# Revit family: WashBasin-Monoblock-Vitra_PluralSeries_7814B003-0001
name_source: partatom
category: Plumbing Fixtures
revit_build: Autodesk Revit 2017 (Build: 20160225_1515(x64)
units: mm (PartAtom-declared; Revit-internal decimal feet)

## family parameters
Cut with Voids When Loaded = No
Host = Face
OmniClass Number = 23.45.05.14.14
OmniClass Title = Sinks/Lavatories
Part Type = Normal
Room Calculation Point = No
Round Connector Dimension = Use Diameter
Shared = Yes

## types (10) — shared parameters
BIMobject category = Sanitary - Basins
CW Connection = No
Default Elevation = 850 mm  [stored 2.78871 ft]
Design country = Turkey
HW Connection = No
IFC Classification = Sanitary Terminal
Main Material = Ceramic
Manufacturer = Vitra
Manufacturer name = Vitra
Masterformat 2014 Code = 22 41 16
Masterformat 2014 Description = Residential Lavatories and Sinks
MountingType = Countertop
NBS Referans Code = 35-65-70-94
NBS Referans Description = Wash Basin Systems
Nominal Depth = 526 mm
NominalHeight = 847 mm
NominalWidth = 492 mm
OmniClass Code = 23.45.05.14.14
OmniClass Description = Sinks/Lavatories
Product certification = https://vitraglobal.com
Product family = Countertop WashBasin
Product group = Plural
UNSPSC Code = 301815
Uniclass 1.4 Code = L7212
Uniclass 1.4 Description = Washbasins
Uniclass 2.0 Code = SS-35-65-70-94
Uniclass 2.0 Description = Sanitary Dispensing And Disposal Units
Uniclass 2015 Code = Pr_40_20_96_81
Uniclass 2015 Name = Wash basins, Sinks and troughs
Uniformat II Code = D2010
Uniformat II Description = Plumbing Fixtures
Vent Connection = No
Warranty Period (Year) = 10 Years
Waste Connection = Yes
Weight Net (kg) = 52,05
Youtube = https://www.youtube.com
zero-valued in all types: Cost

## per-type parameters (varying)
| type | Article No. (default) | Color | Description | Model | Product SKU | Product data url | Product url | Secondary Material | URL |
| WashBasin-Monoblock_Vitra_Plural_(White)_7814B403-0001 | 7814B403-0001 | White | VitrA Plural Monoblock Washbasin 50 cm, with tap hole, | 7814B403-0001 | 7814B403-0001 |  | https://www.vitra.com.tr | Vitra-Ceramic-White | https://vitraglobal.com |
| WashBasin-Monoblock_Vitra_Plural_(MatteWhite)_7814B401-0001 | 7814B401-0001 | Matte White | VitrA Plural | 7814B401-0001 | 7814B401-0001 | https://www.vitra.com.tr |  | Vitra-MatteWhite | https://vitraglobal.com |
| WashBasin-Monoblock_Vitra_Plural_(MatteBeige)_7814B420-0001 | 7814B420-0001 | Matte Beige | VitrA Plural | 7814B420-0001 | 7814B420-0001 | https://www.vitra.com.tr |  | Vitra-MatteBeige | https://www.vitra.com.tr |
| WashBasin-Monoblock_Vitra_Plural_(MatteMink)_7814B450-0001 | 7814B450-0001 | Matte Mink | VitrA Plural | 7814B450-0001 | 7814B450-0001 | https://www.vitra.com.tr |  | Vitra-MatteMink | https://www.vitra.com.tr |
| WashBasin-Monoblock_Vitra_Plural_(MatteBlack)_7814B483-0001 | 7814B483-0001 | Matte Black | VitrA Plural | 7814B483-0001 | 7814B483-0001 | https://www.vitra.com.tr |  | Vitra-MatteBlack | https://www.vitra.com.tr |
| WashBasin-Monoblock_Vitra_Plural_(White)_7814B003-0041 | 7814B003-0041 | White | VitrA Plural | 7814B003-0041 | 7814B003-0041 |  | https://www.vitra.com.tr | Vitra-Ceramic-White | https://vitraglobal.com |
| WashBasin-Monoblock_Vitra_Plural_(MatteWhite)_7814B401-0041 | 7814B401-0041 | Matte White | VitrA Plural | 7814B401-0041 | 7814B401-0041 |  | https://www.vitraglobal.com | Vitra-MatteWhite | https://vitraglobal.com |
| WashBasin-Monoblock_Vitra_Plural_(MatteBeige)_7814B420-0041 | 7814B420-0041 | Matte Beige | VitrA Plural | 7814B420-0041 | 7814B420-0041 |  | https://www.vitraglobal.com | Vitra-MatteBeige | https://www.vitra.com.tr |
| WashBasin-Monoblock_Vitra_Plural_(MatteBlack)_7814B483-0041 | 7814B483-0041 | Matte Black | VitrA Plural | 7814B483-0041 | 7814B483-0041 |  | https://www.vitraglobal.com | Vitra-MatteBlack | https://www.vitra.com.tr |
| WashBasin-Monoblock_Vitra_Plural_(MatteMink)_7814B450-0041 | 7814B450-0041 | Matte Mink | VitrA Plural | 7814B450-0041 | 7814B450-0041 |  | https://www.vitraglobal.com | Vitra-MatteMink | https://www.vitra.com.tr |

note: [stored X ft] marks values corroborated as IEEE doubles in the binary element streams (Revit-internal decimal feet)

## geometry (parser evidence)
native form markers: Sweep x3
no freeform markers — native parametric forms only
